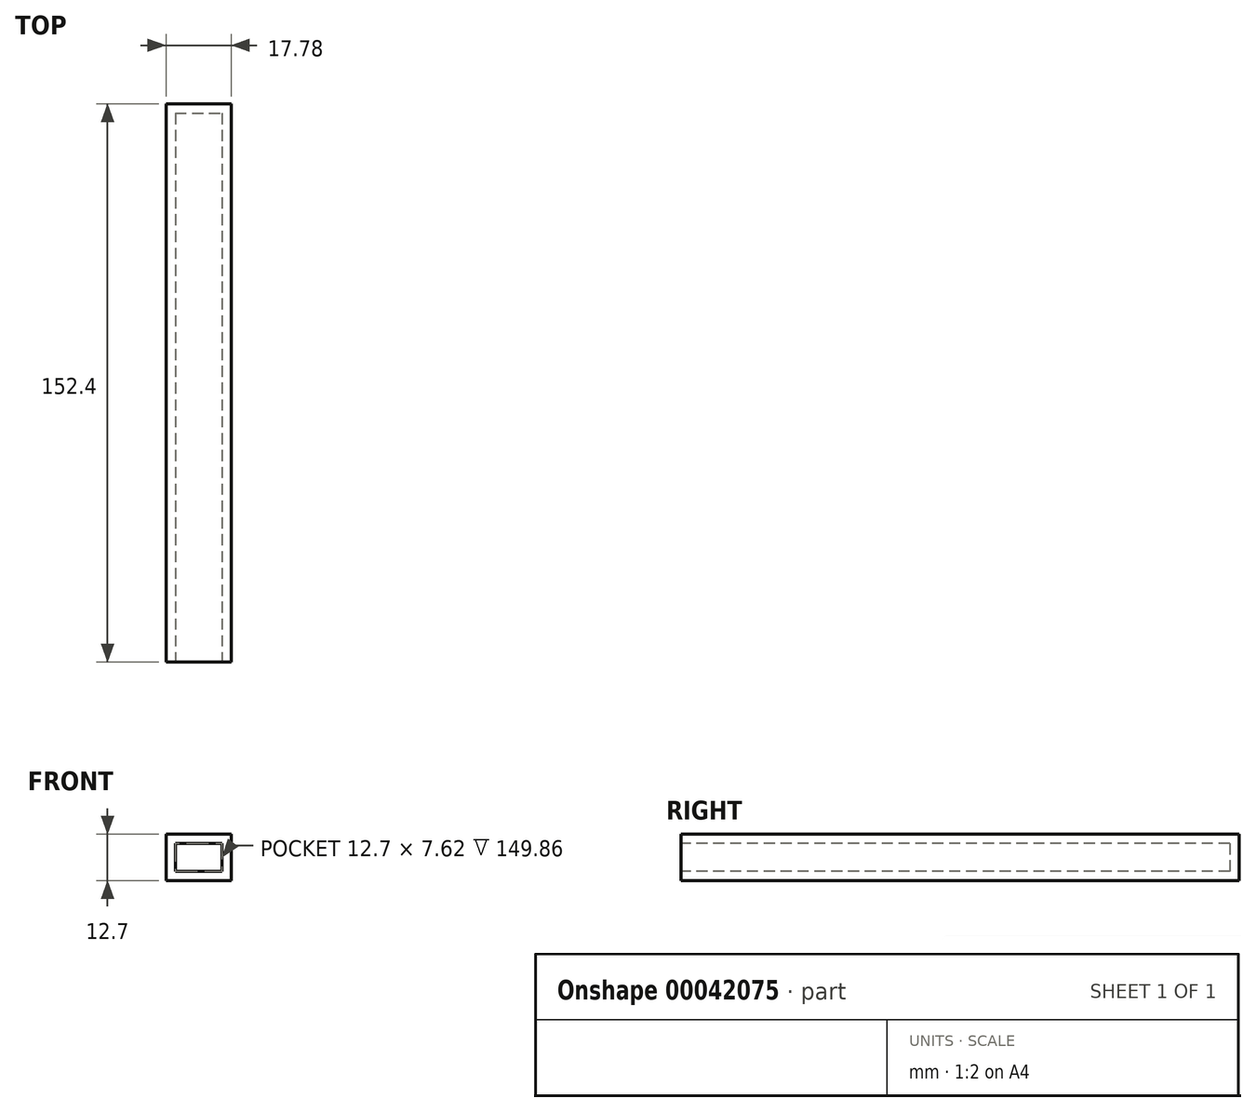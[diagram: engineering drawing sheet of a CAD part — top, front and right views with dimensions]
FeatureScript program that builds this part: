
annotation { "Feature Type Name" : "Feature", "Feature Type Description" : "" }
export const myFeature = defineFeature(function(context is Context, id is Id, definition is map)
    precondition{}
    {
        {
            var Q0;
            Q0=qCreatedBy(makeId("Top.planeOp"),FACE);
            var sketch = newSketch(context, id + "F0", { "sketchPlane" : qUnion([Q0])});
            skLineSegment(sketch, "E0.bottom", {"start": v(-8.9, 76.2) * mm, "end": v(8.9, 76.2) * mm});
            skLineSegment(sketch, "E0.top", {"start": v(-8.89, -76.2) * mm, "end": v(8.9, -76.2) * mm});
            skLineSegment(sketch, "E0.left", {"start": v(-8.9, 76.2) * mm, "end": v(-8.9, -76.2) * mm});
            skLineSegment(sketch, "E0.right", {"start": v(8.9, 76.2) * mm, "end": v(8.9, -76.2) * mm});
            skSolve(sketch);
        }
        {
            var Q0;
            Q0=makeQuery(id+"F0.imprint","IMPRINT",FACE,{"disambiguationData":[TD([[makeQuery(id+"F0.imprint","IMPRINT",EDGE,{"derivedFrom":sQuery(id+"F0.wireOp",EDGE,"E0.bottom")}),-1.0]])]});
            extrude(context, id + "F1", {"entities" : qUnion([Q0]), "depth" : 12.7 * mm});
        }
        {
            var Q0;
            Q0=makeQuery(id+"F1.opExtrude","SWEPT_FACE",FACE,{"disambiguationData":[OSD([sQuery(id+"F0.wireOp",EDGE,"E0.top")])]});
            shell(context, id + "F2", {"entities" : qUnion([Q0]), "thickness" : 2.54 * mm});
        }
    });
